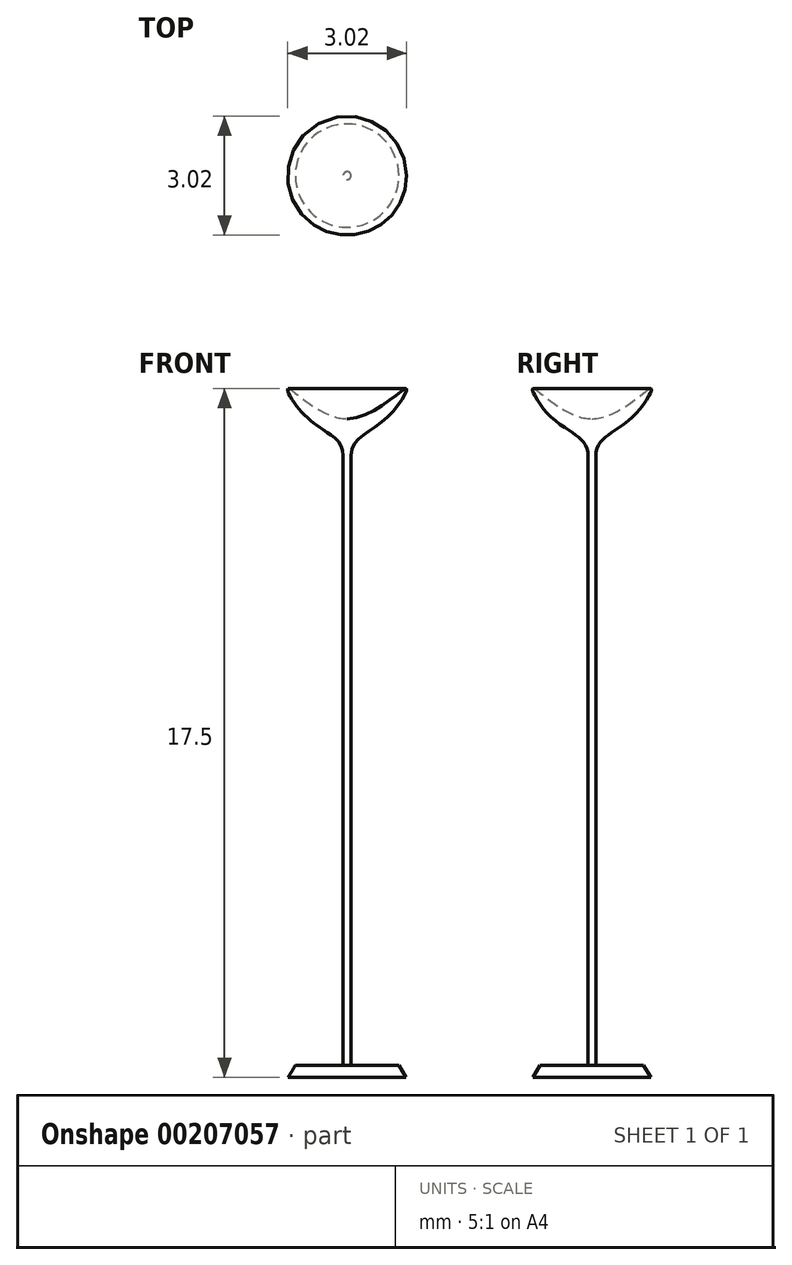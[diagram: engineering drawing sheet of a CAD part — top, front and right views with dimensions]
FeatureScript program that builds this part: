
annotation { "Feature Type Name" : "Feature", "Feature Type Description" : "" }
export const myFeature = defineFeature(function(context is Context, id is Id, definition is map)
    precondition{}
    {
        {
            var Q0;
            Q0=qCreatedBy(makeId("Front.planeOp"),FACE);
            var sketch = newSketch(context, id + "F0", { "sketchPlane" : qUnion([Q0])});
            skLineSegment(sketch, "E0", {"start": v(0, 0) * mm, "end": v(0, 17.5) * mm, "construction": true});
            skLineSegment(sketch, "E1", {"start": v(0, 0) * mm, "end": v(1.5, 0) * mm});
            skLineSegment(sketch, "E2", {"start": v(1.5, 0) * mm, "end": v(1.31, 0.3) * mm});
            skLineSegment(sketch, "E3", {"start": v(1.31, 0.3) * mm, "end": v(0.1, 0.3) * mm});
            skLineSegment(sketch, "E4", {"start": v(0.1, 0.3) * mm, "end": v(0.1, 15.8) * mm});
            skFitSpline(sketch, "E5", {"points": [v(0.1, 15.8) * mm, v(0.97, 16.72) * mm, v(1.5, 17.5) * mm, v(0, 16.73) * mm], "startDerivative": vector(0, 4.18) * mm, "endDerivative": vector(-5.38, 0) * mm});
            skLineSegment(sketch, "E6", {"start": v(0, 16.73) * mm, "end": v(0, 0) * mm});
            skSolve(sketch);
        }
        {
            var Q0;
            Q0=makeQuery(id+"F0.imprint","IMPRINT",FACE,{"disambiguationData":[TD([[makeQuery(id+"F0.imprint","IMPRINT",EDGE,{"derivedFrom":sQuery(id+"F0.wireOp",EDGE,"E1")}),1.0]])]});
            var Q1;
            Q1=sQuery(id+"F0.wireOp",EDGE,"E0");
            revolve(context, id + "F1", {"entities" : qUnion([Q0]), "axis" : qUnion([Q1]), "revolveType" : RevolveType.FULL});
        }
    });
